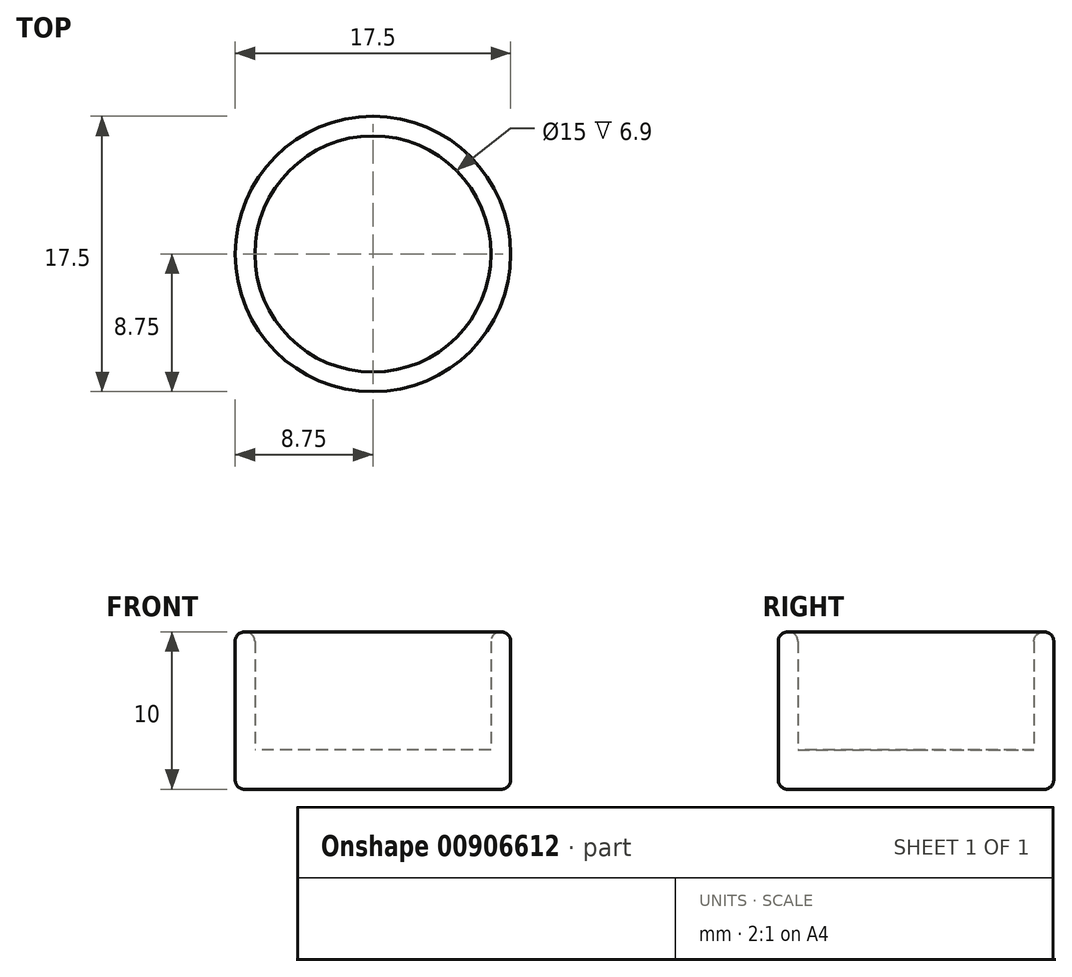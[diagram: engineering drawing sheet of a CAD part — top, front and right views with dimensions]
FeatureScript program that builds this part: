
annotation { "Feature Type Name" : "Feature", "Feature Type Description" : "" }
export const myFeature = defineFeature(function(context is Context, id is Id, definition is map)
    precondition{}
    {
        {
            var Q0;
            Q0=qCreatedBy(makeId("Top.planeOp"),FACE);
            var sketch = newSketch(context, id + "F0", { "sketchPlane" : qUnion([Q0])});
            skCircle(sketch, "E0", {"center": v(0, 0) * mm, "radius": 7.5 * mm});
            skCircle(sketch, "E1", {"center": v(0, 0) * mm, "radius": 8.75 * mm});
            skSolve(sketch);
        }
        {
            var Q0;
            Q0=makeQuery(id+"F0.imprint","IMPRINT",FACE,{"disambiguationData":[TD([[makeQuery(id+"F0.imprint","IMPRINT",EDGE,{"derivedFrom":sQuery(id+"F0.wireOp",EDGE,"E0")}),1.0]])]});
            extrude(context, id + "F1", {"entities" : qUnion([Q0]), "depth" : 2.5 * mm, "offsetDistance" : 25 * mm});
        }
        {
            var Q0;
            Q0 = qSketchRegion(id + "F0", true);
            extrude(context, id + "F2", {"entities" : qUnion([Q0]), "operationType" : NewBodyOperationType.ADD, "depth" : 10 * mm, "offsetDistance" : 25 * mm});
        }
        {
            var Q0;
            Q0=makeQuery(id+"F2.opExtrude","CAP_EDGE",EDGE,{"disambiguationData":[OSD([sQuery(id+"F0.wireOp",EDGE,"E0")])],"isStart":false});
            var Q1;
            Q1=makeQuery(id+"F2.opExtrude","CAP_EDGE",EDGE,{"disambiguationData":[OSD([sQuery(id+"F0.wireOp",EDGE,"E1")])],"isStart":false});
            var Q2;
            Q2=makeQuery(id+"F2.opExtrude","CAP_EDGE",EDGE,{"disambiguationData":[OSD([sQuery(id+"F0.wireOp",EDGE,"E1")])],"isStart":true});
            fillet(context, id + "F3", {"entities" : qUnion([Q0, Q1, Q2]), "radius" : .6 * mm, "tangentPropagation" : true, "allowEdgeOverflow" : false});
        }
    });
